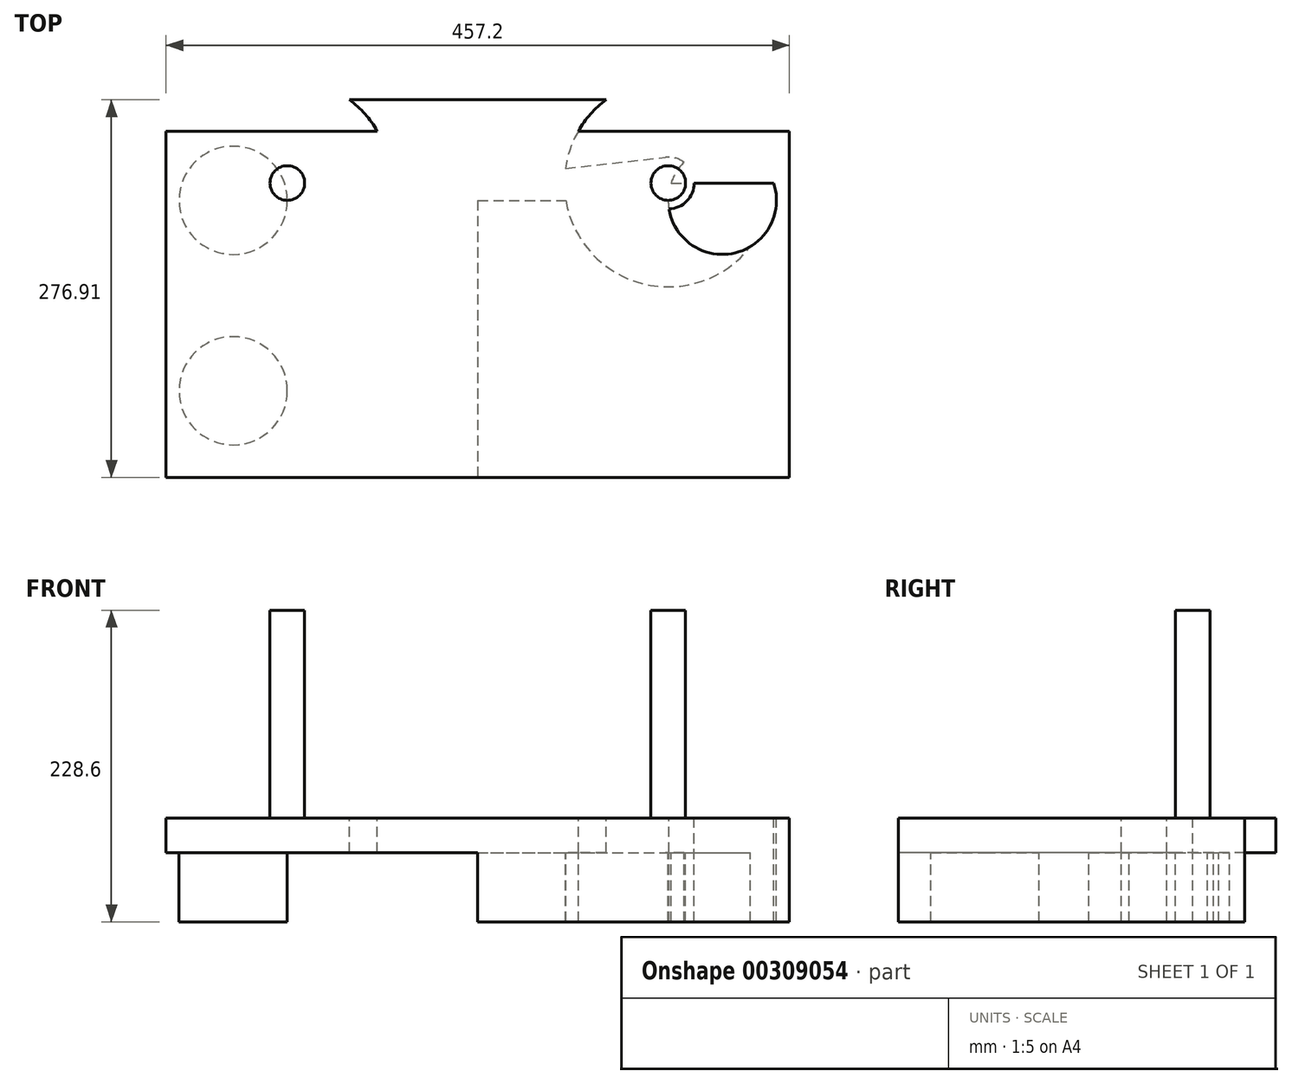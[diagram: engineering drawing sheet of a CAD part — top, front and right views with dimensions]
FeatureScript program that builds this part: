
annotation { "Feature Type Name" : "Feature", "Feature Type Description" : "" }
export const myFeature = defineFeature(function(context is Context, id is Id, definition is map)
    precondition{}
    {
        {
            var Q0;
            Q0=qCreatedBy(makeId("Top.planeOp"),FACE);
            var sketch = newSketch(context, id + "F0", { "sketchPlane" : qUnion([Q0])});
            skLineSegment(sketch, "E0", {"start": v(-140.58, 0) * mm, "end": v(0, 0) * mm});
            skLineSegment(sketch, "E1", {"start": v(0, 0) * mm, "end": v(140.58, 0) * mm});
            skLineSegment(sketch, "E2", {"start": v(0, 0) * mm, "end": v(139.7, 15.67) * mm});
            skLineSegment(sketch, "E3", {"start": v(0, 0) * mm, "end": v(-139.7, 15.67) * mm});
            skLineSegment(sketch, "E4.0", {"start": v(0, -57.5) * mm, "end": v(146.07, -41.12) * mm});
            skLineSegment(sketch, "E4.1", {"start": v(0, -57.5) * mm, "end": v(-146.07, -41.12) * mm});
            skLineSegment(sketch, "E5.0", {"start": v(0, 57.5) * mm, "end": v(-133.33, 72.46) * mm});
            skLineSegment(sketch, "E5.1", {"start": v(0, 57.5) * mm, "end": v(133.33, 72.46) * mm});
            skArc(sketch, "E6", {"start": v(-69.27, 108.43) * mm, "mid": v(0, 0.48) * mm, "end": v(69.27, 108.43) * mm});
            skCircle(sketch, "E7", {"center": v(0, 76.68) * mm, "radius": 19.05 * mm});
            skCircle(sketch, "E8", {"center": v(139.7, -61) * mm, "radius": 76.2 * mm});
            skCircle(sketch, "E9", {"center": v(-139.7, -61) * mm, "radius": 76.2 * mm});
            skCircle(sketch, "E10", {"center": v(139.7, -61) * mm, "radius": 19.05 * mm});
            skCircle(sketch, "E11", {"center": v(-139.7, -61) * mm, "radius": 19.05 * mm});
            skLineSegment(sketch, "E12", {"start": v(-139.7, 15.67) * mm, "end": v(139.7, 15.67) * mm});
            skCircle(sketch, "E13", {"center": v(0, 76.68) * mm, "radius": 12.7 * mm});
            skCircle(sketch, "E14", {"center": v(-139.7, -61) * mm, "radius": 12.7 * mm});
            skCircle(sketch, "E15", {"center": v(139.7, -61) * mm, "radius": 12.7 * mm});
            skLineSegment(sketch, "E16.bottom", {"start": v(-228.6, -22.9) * mm, "end": v(228.6, -22.9) * mm});
            skLineSegment(sketch, "E16.top", {"start": v(-228.6, -276.9) * mm, "end": v(228.6, -276.9) * mm});
            skLineSegment(sketch, "E16.left", {"start": v(-228.6, -22.9) * mm, "end": v(-228.6, -276.9) * mm});
            skLineSegment(sketch, "E16.right", {"start": v(228.6, -22.9) * mm, "end": v(228.6, -276.9) * mm});
            skLineSegment(sketch, "E17", {"start": v(-228.6, -61) * mm, "end": v(-139.7, -61) * mm});
            skLineSegment(sketch, "E18", {"start": v(139.7, -61) * mm, "end": v(228.6, -61) * mm});
            skLineSegment(sketch, "E19", {"start": v(0, -22.9) * mm, "end": v(0, -276.9) * mm});
            skLineSegment(sketch, "E20", {"start": v(-179.39, -73.7) * mm, "end": v(179.39, -73.7) * mm});
            skPoint(sketch, "E21", {"position": v(0, -73.7) * mm});
            skCircle(sketch, "E22", {"center": v(-179.39, -73.7) * mm, "radius": 39.69 * mm});
            skCircle(sketch, "E23", {"center": v(179.39, -73.7) * mm, "radius": 39.69 * mm});
            skLineSegment(sketch, "E24", {"start": v(-179.39, -213.4) * mm, "end": v(0, -213.4) * mm});
            skLineSegment(sketch, "E25", {"start": v(0, -213.4) * mm, "end": v(179.39, -213.4) * mm});
            skCircle(sketch, "E26", {"center": v(-179.39, -213.4) * mm, "radius": 39.69 * mm});
            skCircle(sketch, "E27", {"center": v(179.39, -213.4) * mm, "radius": 39.69 * mm});
            skLineSegment(sketch, "E28", {"start": v(294.3, 2.5) * mm, "end": v(418.12, 2.5) * mm});
            skLineSegment(sketch, "E29", {"start": v(-69.27, 108.43) * mm, "end": v(-30.16, 108.43) * mm});
            skLineSegment(sketch, "E30", {"start": v(-30.16, 108.43) * mm, "end": v(-30.16, 127.48) * mm});
            skLineSegment(sketch, "E31", {"start": v(-30.16, 127.48) * mm, "end": v(30.16, 127.48) * mm});
            skLineSegment(sketch, "E32", {"start": v(30.16, 127.48) * mm, "end": v(30.16, 108.43) * mm});
            skLineSegment(sketch, "E33", {"start": v(0, 108.43) * mm, "end": v(0, 127.48) * mm, "construction": true});
            skLineSegment(sketch, "E34.trimOffspring", {"start": v(30.16, 108.43) * mm, "end": v(69.27, 108.43) * mm});
            skSolve(sketch);
        }
        {
            var Q0;
            {var subQ0=sQuery(id+"F0.wireOp",EDGE,"E16.bottom");var subQ1=sQuery(id+"F0.wireOp",EDGE,"E8");var subQ2=makeQuery(id+"F0.imprint","INTERSECT",VERTEX,{"disambiguationData":[OD(0.0)],"derivedFrom":[subQ1,subQ0]});Q0=makeQuery(id+"F0.imprint","IMPRINT",FACE,{"disambiguationData":[TD([[makeQuery(id+"F0.imprint","IMPRINT",EDGE,{"disambiguationData":[TD([[subQ2,1.0]])],"derivedFrom":subQ1}),-1.0]])]});}
            var Q1;
            Q1=makeQuery(id+"F0.imprint","IMPRINT",FACE,{"disambiguationData":[TD([[makeQuery(id+"F0.imprint","IMPRINT",EDGE,{"derivedFrom":sQuery(id+"F0.wireOp",EDGE,"E27")}),-1.0]])]});
            var Q2;
            Q2=makeQuery(id+"F0.imprint","IMPRINT",FACE,{"disambiguationData":[TD([[makeQuery(id+"F0.imprint","IMPRINT",EDGE,{"derivedFrom":sQuery(id+"F0.wireOp",EDGE,"E26")}),-1.0]])]});
            var Q3;
            {var subQ0=sQuery(id+"F0.wireOp",EDGE,"E20");var subQ1=sQuery(id+"F0.wireOp",EDGE,"E8");var subQ2=makeQuery(id+"F0.imprint","INTERSECT",VERTEX,{"derivedFrom":[subQ1,subQ0]});Q3=makeQuery(id+"F0.imprint","IMPRINT",FACE,{"disambiguationData":[TD([[makeQuery(id+"F0.imprint","IMPRINT",EDGE,{"disambiguationData":[TD([[subQ2,-1.0]])],"derivedFrom":subQ1}),1.0]])]});}
            var Q4;
            {var subQ0=sQuery(id+"F0.wireOp",EDGE,"E23");var subQ1=sQuery(id+"F0.wireOp",EDGE,"E8");var subQ2=makeQuery(id+"F0.imprint","INTERSECT",VERTEX,{"disambiguationData":[OD(0.0)],"derivedFrom":[subQ1,subQ0]});Q4=makeQuery(id+"F0.imprint","IMPRINT",FACE,{"disambiguationData":[TD([[makeQuery(id+"F0.imprint","IMPRINT",EDGE,{"disambiguationData":[TD([[subQ2,-1.0]])],"derivedFrom":subQ1}),1.0]])]});}
            var Q5;
            Q5=makeQuery(id+"F0.imprint","IMPRINT",FACE,{"disambiguationData":[TD([[makeQuery(id+"F0.imprint","IMPRINT",EDGE,{"derivedFrom":sQuery(id+"F0.wireOp",EDGE,"E27")}),1.0]])]});
            var Q6;
            Q6=makeQuery(id+"F0.imprint","IMPRINT",FACE,{"disambiguationData":[TD([[makeQuery(id+"F0.imprint","IMPRINT",EDGE,{"derivedFrom":sQuery(id+"F0.wireOp",EDGE,"E26")}),1.0]])]});
            var Q7;
            {var subQ0=sQuery(id+"F0.wireOp",EDGE,"E23");var subQ1=sQuery(id+"F0.wireOp",EDGE,"E8");var subQ2=makeQuery(id+"F0.imprint","INTERSECT",VERTEX,{"disambiguationData":[OD(0.0)],"derivedFrom":[subQ1,subQ0]});Q7=makeQuery(id+"F0.imprint","IMPRINT",FACE,{"disambiguationData":[TD([[makeQuery(id+"F0.imprint","IMPRINT",EDGE,{"disambiguationData":[TD([[subQ2,-1.0]])],"derivedFrom":subQ1}),-1.0]])]});}
            var Q8;
            {var subQ0=sQuery(id+"F0.wireOp",EDGE,"E22");var subQ1=sQuery(id+"F0.wireOp",EDGE,"E9");var subQ2=makeQuery(id+"F0.imprint","INTERSECT",VERTEX,{"disambiguationData":[OD(0.0)],"derivedFrom":[subQ1,subQ0]});Q8=makeQuery(id+"F0.imprint","IMPRINT",FACE,{"disambiguationData":[TD([[makeQuery(id+"F0.imprint","IMPRINT",EDGE,{"disambiguationData":[TD([[subQ2,-1.0]])],"derivedFrom":subQ1}),-1.0]])]});}
            var Q9;
            {var subQ0=sQuery(id+"F0.wireOp",EDGE,"E16.bottom");var subQ1=sQuery(id+"F0.wireOp",EDGE,"E9");var subQ2=makeQuery(id+"F0.imprint","INTERSECT",VERTEX,{"disambiguationData":[OD(0.0)],"derivedFrom":[subQ1,subQ0]});Q9=makeQuery(id+"F0.imprint","IMPRINT",FACE,{"disambiguationData":[TD([[makeQuery(id+"F0.imprint","IMPRINT",EDGE,{"disambiguationData":[TD([[subQ2,-1.0]])],"derivedFrom":subQ1}),-1.0]])]});}
            var Q10;
            {var subQ1=sQuery(id+"F0.wireOp",EDGE,"E4.1");var subQ3=sQuery(id+"F0.wireOp",EDGE,"E9");var subQ4=makeQuery(id+"F0.imprint","INTERSECT",VERTEX,{"derivedFrom":[subQ1,subQ3]});Q10=makeQuery(id+"F0.imprint","IMPRINT",FACE,{"disambiguationData":[TD([[makeQuery(id+"F0.imprint","IMPRINT",EDGE,{"disambiguationData":[TD([[subQ4,1.0]])],"derivedFrom":subQ3}),-1.0]])]});}
            var Q11;
            {var subQ1=sQuery(id+"F0.wireOp",EDGE,"E4.0");var subQ3=sQuery(id+"F0.wireOp",EDGE,"E8");var subQ4=makeQuery(id+"F0.imprint","INTERSECT",VERTEX,{"derivedFrom":[subQ1,subQ3]});Q11=makeQuery(id+"F0.imprint","IMPRINT",FACE,{"disambiguationData":[TD([[makeQuery(id+"F0.imprint","IMPRINT",EDGE,{"disambiguationData":[TD([[subQ4,-1.0]])],"derivedFrom":subQ3}),-1.0]])]});}
            var Q12;
            {var subQ5=sQuery(id+"F0.wireOp",EDGE,"E10");var subQ6=sQuery(id+"F0.wireOp",EDGE,"E4.0");var subQ7=makeQuery(id+"F0.imprint","INTERSECT",VERTEX,{"derivedFrom":[subQ6,subQ5]});Q12=makeQuery(id+"F0.imprint","IMPRINT",FACE,{"disambiguationData":[TD([[makeQuery(id+"F0.imprint","IMPRINT",EDGE,{"disambiguationData":[TD([[subQ7,1.0]])],"derivedFrom":subQ6}),-1.0]])]});}
            var Q13;
            {var subQ0=sQuery(id+"F0.wireOp",EDGE,"E10");var subQ1=sQuery(id+"F0.wireOp",EDGE,"E4.0");var subQ2=makeQuery(id+"F0.imprint","INTERSECT",VERTEX,{"derivedFrom":[subQ1,subQ0]});Q13=makeQuery(id+"F0.imprint","IMPRINT",FACE,{"disambiguationData":[TD([[makeQuery(id+"F0.imprint","IMPRINT",EDGE,{"disambiguationData":[TD([[subQ2,1.0]])],"derivedFrom":subQ1}),1.0]])]});}
            var Q14;
            {var subQ1=sQuery(id+"F0.wireOp",EDGE,"E4.0");var subQ3=sQuery(id+"F0.wireOp",EDGE,"E8");var subQ4=makeQuery(id+"F0.imprint","INTERSECT",VERTEX,{"derivedFrom":[subQ1,subQ3]});Q14=makeQuery(id+"F0.imprint","IMPRINT",FACE,{"disambiguationData":[TD([[makeQuery(id+"F0.imprint","IMPRINT",EDGE,{"disambiguationData":[TD([[subQ4,1.0]])],"derivedFrom":subQ3}),-1.0]])]});}
            var Q15;
            {var subQ1=sQuery(id+"F0.wireOp",EDGE,"E4.1");var subQ3=sQuery(id+"F0.wireOp",EDGE,"E9");var subQ4=makeQuery(id+"F0.imprint","INTERSECT",VERTEX,{"derivedFrom":[subQ1,subQ3]});Q15=makeQuery(id+"F0.imprint","IMPRINT",FACE,{"disambiguationData":[TD([[makeQuery(id+"F0.imprint","IMPRINT",EDGE,{"disambiguationData":[TD([[subQ4,-1.0]])],"derivedFrom":subQ3}),-1.0]])]});}
            var Q16;
            {var subQ0=sQuery(id+"F0.wireOp",EDGE,"E11");var subQ1=sQuery(id+"F0.wireOp",EDGE,"E4.1");var subQ2=makeQuery(id+"F0.imprint","INTERSECT",VERTEX,{"derivedFrom":[subQ1,subQ0]});Q16=makeQuery(id+"F0.imprint","IMPRINT",FACE,{"disambiguationData":[TD([[makeQuery(id+"F0.imprint","IMPRINT",EDGE,{"disambiguationData":[TD([[subQ2,1.0]])],"derivedFrom":subQ1}),-1.0]])]});}
            var Q17;
            {var subQ0=sQuery(id+"F0.wireOp",EDGE,"E11");var subQ1=sQuery(id+"F0.wireOp",EDGE,"E4.1");var subQ2=makeQuery(id+"F0.imprint","INTERSECT",VERTEX,{"derivedFrom":[subQ1,subQ0]});Q17=makeQuery(id+"F0.imprint","IMPRINT",FACE,{"disambiguationData":[TD([[makeQuery(id+"F0.imprint","IMPRINT",EDGE,{"disambiguationData":[TD([[subQ2,1.0]])],"derivedFrom":subQ1}),1.0]])]});}
            var Q18;
            {var subQ0=sQuery(id+"F0.wireOp",EDGE,"E22");var subQ1=sQuery(id+"F0.wireOp",EDGE,"E9");var subQ2=makeQuery(id+"F0.imprint","INTERSECT",VERTEX,{"disambiguationData":[OD(1.0)],"derivedFrom":[subQ1,subQ0]});Q18=makeQuery(id+"F0.imprint","IMPRINT",FACE,{"disambiguationData":[TD([[makeQuery(id+"F0.imprint","IMPRINT",EDGE,{"disambiguationData":[TD([[subQ2,-1.0]])],"derivedFrom":subQ1}),1.0]])]});}
            var Q19;
            {var subQ0=sQuery(id+"F0.wireOp",EDGE,"E22");var subQ1=sQuery(id+"F0.wireOp",EDGE,"E9");var subQ2=makeQuery(id+"F0.imprint","INTERSECT",VERTEX,{"disambiguationData":[OD(0.0)],"derivedFrom":[subQ1,subQ0]});Q19=makeQuery(id+"F0.imprint","IMPRINT",FACE,{"disambiguationData":[TD([[makeQuery(id+"F0.imprint","IMPRINT",EDGE,{"disambiguationData":[TD([[subQ2,-1.0]])],"derivedFrom":subQ1}),1.0]])]});}
            var Q20;
            Q20=makeQuery(id+"F0.imprint","IMPRINT",FACE,{"disambiguationData":[TD([[makeQuery(id+"F0.imprint","IMPRINT",EDGE,{"derivedFrom":sQuery(id+"F0.wireOp",EDGE,"E14")}),-1.0]])]});
            var Q21;
            Q21=makeQuery(id+"F0.imprint","IMPRINT",FACE,{"disambiguationData":[TD([[makeQuery(id+"F0.imprint","IMPRINT",EDGE,{"derivedFrom":sQuery(id+"F0.wireOp",EDGE,"E14")}),1.0]])]});
            var Q22;
            Q22=makeQuery(id+"F0.imprint","IMPRINT",FACE,{"disambiguationData":[TD([[makeQuery(id+"F0.imprint","IMPRINT",EDGE,{"derivedFrom":sQuery(id+"F0.wireOp",EDGE,"E15")}),-1.0]])]});
            var Q23;
            Q23=makeQuery(id+"F0.imprint","IMPRINT",FACE,{"disambiguationData":[TD([[makeQuery(id+"F0.imprint","IMPRINT",EDGE,{"derivedFrom":sQuery(id+"F0.wireOp",EDGE,"E15")}),1.0]])]});
            var Q24;
            {var subQ0=sQuery(id+"F0.wireOp",EDGE,"E17");var subQ1=sQuery(id+"F0.wireOp",EDGE,"E9");var subQ2=makeQuery(id+"F0.imprint","INTERSECT",VERTEX,{"derivedFrom":[subQ1,subQ0]});Q24=makeQuery(id+"F0.imprint","IMPRINT",FACE,{"disambiguationData":[TD([[makeQuery(id+"F0.imprint","IMPRINT",EDGE,{"disambiguationData":[TD([[subQ2,-1.0]])],"derivedFrom":subQ1}),1.0]])]});}
            var Q25;
            {var subQ0=sQuery(id+"F0.wireOp",EDGE,"E17");var subQ1=sQuery(id+"F0.wireOp",EDGE,"E9");var subQ2=makeQuery(id+"F0.imprint","INTERSECT",VERTEX,{"derivedFrom":[subQ1,subQ0]});Q25=makeQuery(id+"F0.imprint","IMPRINT",FACE,{"disambiguationData":[TD([[makeQuery(id+"F0.imprint","IMPRINT",EDGE,{"disambiguationData":[TD([[subQ2,-1.0]])],"derivedFrom":subQ1}),-1.0]])]});}
            var Q26;
            {var subQ1=sQuery(id+"F0.wireOp",EDGE,"E11");var subQ7=makeQuery(id+"F0.imprint","INTERSECT",VERTEX,{"derivedFrom":[sQuery(id+"F0.wireOp",EDGE,"E4.1"),subQ1]});Q26=makeQuery(id+"F0.imprint","IMPRINT",FACE,{"disambiguationData":[TD([[makeQuery(id+"F0.imprint","IMPRINT",EDGE,{"disambiguationData":[TD([[subQ7,-1.0]])],"derivedFrom":subQ1}),1.0]])]});}
            var Q27;
            {var subQ0=sQuery(id+"F0.wireOp",EDGE,"E22");var subQ1=sQuery(id+"F0.wireOp",EDGE,"E11");var subQ2=makeQuery(id+"F0.imprint","INTERSECT",VERTEX,{"disambiguationData":[OD(1.0)],"derivedFrom":[subQ1,subQ0]});Q27=makeQuery(id+"F0.imprint","IMPRINT",FACE,{"disambiguationData":[TD([[makeQuery(id+"F0.imprint","IMPRINT",EDGE,{"disambiguationData":[TD([[subQ2,-1.0]])],"derivedFrom":subQ1}),1.0]])]});}
            var Q28;
            {var subQ1=sQuery(id+"F0.wireOp",EDGE,"E10");var subQ7=makeQuery(id+"F0.imprint","INTERSECT",VERTEX,{"derivedFrom":[sQuery(id+"F0.wireOp",EDGE,"E4.0"),subQ1]});Q28=makeQuery(id+"F0.imprint","IMPRINT",FACE,{"disambiguationData":[TD([[makeQuery(id+"F0.imprint","IMPRINT",EDGE,{"disambiguationData":[TD([[subQ7,1.0]])],"derivedFrom":subQ1}),1.0]])]});}
            var Q29;
            {var subQ0=sQuery(id+"F0.wireOp",EDGE,"E20");var subQ1=sQuery(id+"F0.wireOp",EDGE,"E11");var subQ2=makeQuery(id+"F0.imprint","INTERSECT",VERTEX,{"disambiguationData":[OD(0.0)],"derivedFrom":[subQ1,subQ0]});Q29=makeQuery(id+"F0.imprint","IMPRINT",FACE,{"disambiguationData":[TD([[makeQuery(id+"F0.imprint","IMPRINT",EDGE,{"disambiguationData":[TD([[subQ2,-1.0]])],"derivedFrom":subQ1}),1.0]])]});}
            var Q30;
            {var subQ0=sQuery(id+"F0.wireOp",EDGE,"E20");var subQ1=sQuery(id+"F0.wireOp",EDGE,"E10");var subQ2=makeQuery(id+"F0.imprint","INTERSECT",VERTEX,{"disambiguationData":[OD(1.0)],"derivedFrom":[subQ1,subQ0]});Q30=makeQuery(id+"F0.imprint","IMPRINT",FACE,{"disambiguationData":[TD([[makeQuery(id+"F0.imprint","IMPRINT",EDGE,{"disambiguationData":[TD([[subQ2,-1.0]])],"derivedFrom":subQ1}),1.0]])]});}
            var Q31;
            {var subQ0=sQuery(id+"F0.wireOp",EDGE,"E20");var subQ1=sQuery(id+"F0.wireOp",EDGE,"E10");var subQ2=makeQuery(id+"F0.imprint","INTERSECT",VERTEX,{"disambiguationData":[OD(0.0)],"derivedFrom":[subQ1,subQ0]});Q31=makeQuery(id+"F0.imprint","IMPRINT",FACE,{"disambiguationData":[TD([[makeQuery(id+"F0.imprint","IMPRINT",EDGE,{"disambiguationData":[TD([[subQ2,1.0]])],"derivedFrom":subQ1}),1.0]])]});}
            var Q32;
            {var subQ0=sQuery(id+"F0.wireOp",EDGE,"E18");var subQ1=sQuery(id+"F0.wireOp",EDGE,"E8");var subQ2=makeQuery(id+"F0.imprint","INTERSECT",VERTEX,{"derivedFrom":[subQ1,subQ0]});Q32=makeQuery(id+"F0.imprint","IMPRINT",FACE,{"disambiguationData":[TD([[makeQuery(id+"F0.imprint","IMPRINT",EDGE,{"disambiguationData":[TD([[subQ2,-1.0]])],"derivedFrom":subQ1}),1.0]])]});}
            extrude(context, id + "F1", {"entities" : qUnion([Q0, Q1, Q2, Q3, Q4, Q5, Q6, Q7, Q8, Q9, Q10, Q11, Q12, Q13, Q14, Q15, Q16, Q17, Q18, Q19, Q20, Q21, Q22, Q23, Q24, Q25, Q26, Q27, Q28, Q29, Q30, Q31, Q32]), "oppositeDirection" : true, "depth" : 25.4 * mm});
        }
        {
            var Q0;
            {var subQ0=sQuery(id+"F0.wireOp",EDGE,"E18");var subQ1=sQuery(id+"F0.wireOp",EDGE,"E8");var subQ2=makeQuery(id+"F0.imprint","INTERSECT",VERTEX,{"derivedFrom":[subQ1,subQ0]});Q0=makeQuery(id+"F0.imprint","IMPRINT",FACE,{"disambiguationData":[TD([[makeQuery(id+"F0.imprint","IMPRINT",EDGE,{"disambiguationData":[TD([[subQ2,-1.0]])],"derivedFrom":subQ1}),1.0]])]});}
            var Q1;
            {var subQ0=sQuery(id+"F0.wireOp",EDGE,"E18");var subQ1=sQuery(id+"F0.wireOp",EDGE,"E8");var subQ2=makeQuery(id+"F0.imprint","INTERSECT",VERTEX,{"derivedFrom":[subQ1,subQ0]});Q1=makeQuery(id+"F0.imprint","IMPRINT",FACE,{"disambiguationData":[TD([[makeQuery(id+"F0.imprint","IMPRINT",EDGE,{"disambiguationData":[TD([[subQ2,-1.0]])],"derivedFrom":subQ1}),-1.0]])]});}
            var Q2;
            {var subQ0=sQuery(id+"F0.wireOp",EDGE,"E23");var subQ1=sQuery(id+"F0.wireOp",EDGE,"E8");var subQ2=makeQuery(id+"F0.imprint","INTERSECT",VERTEX,{"disambiguationData":[OD(0.0)],"derivedFrom":[subQ1,subQ0]});Q2=makeQuery(id+"F0.imprint","IMPRINT",FACE,{"disambiguationData":[TD([[makeQuery(id+"F0.imprint","IMPRINT",EDGE,{"disambiguationData":[TD([[subQ2,-1.0]])],"derivedFrom":subQ1}),-1.0]])]});}
            var Q3;
            {var subQ1=sQuery(id+"F0.wireOp",EDGE,"E8");var subQ6=sQuery(id+"F0.wireOp",EDGE,"E23");var subQ8=makeQuery(id+"F0.imprint","INTERSECT",VERTEX,{"disambiguationData":[OD(0.0)],"derivedFrom":[subQ1,subQ6]});Q3=makeQuery(id+"F0.imprint","IMPRINT",FACE,{"disambiguationData":[TD([[makeQuery(id+"F0.imprint","IMPRINT",EDGE,{"disambiguationData":[TD([[subQ8,-1.0]])],"derivedFrom":subQ1}),1.0]])]});}
            var Q4;
            {var subQ0=sQuery(id+"F0.wireOp",EDGE,"E20");var subQ1=sQuery(id+"F0.wireOp",EDGE,"E10");var subQ2=makeQuery(id+"F0.imprint","INTERSECT",VERTEX,{"disambiguationData":[OD(0.0)],"derivedFrom":[subQ1,subQ0]});Q4=makeQuery(id+"F0.imprint","IMPRINT",FACE,{"disambiguationData":[TD([[makeQuery(id+"F0.imprint","IMPRINT",EDGE,{"disambiguationData":[TD([[subQ2,-1.0]])],"derivedFrom":subQ1}),1.0]])]});}
            var Q5;
            {var subQ0=sQuery(id+"F0.wireOp",EDGE,"E20");var subQ1=sQuery(id+"F0.wireOp",EDGE,"E10");var subQ2=makeQuery(id+"F0.imprint","INTERSECT",VERTEX,{"disambiguationData":[OD(0.0)],"derivedFrom":[subQ1,subQ0]});Q5=makeQuery(id+"F0.imprint","IMPRINT",FACE,{"disambiguationData":[TD([[makeQuery(id+"F0.imprint","IMPRINT",EDGE,{"disambiguationData":[TD([[subQ2,1.0]])],"derivedFrom":subQ1}),1.0]])]});}
            var Q6;
            {var subQ0=sQuery(id+"F0.wireOp",EDGE,"E18");var subQ3=sQuery(id+"F0.wireOp",EDGE,"E23");var subQ5=makeQuery(id+"F0.imprint","INTERSECT",VERTEX,{"disambiguationData":[OD(0.0)],"derivedFrom":[subQ0,subQ3]});Q6=makeQuery(id+"F0.imprint","IMPRINT",FACE,{"disambiguationData":[TD([[makeQuery(id+"F0.imprint","IMPRINT",EDGE,{"disambiguationData":[TD([[subQ5,-1.0]])],"derivedFrom":subQ0}),-1.0]])]});}
            var Q7;
            {var subQ0=sQuery(id+"F0.wireOp",EDGE,"E23");var subQ1=sQuery(id+"F0.wireOp",EDGE,"E15");var subQ2=makeQuery(id+"F0.imprint","INTERSECT",VERTEX,{"derivedFrom":[subQ1,subQ0]});Q7=makeQuery(id+"F0.imprint","IMPRINT",FACE,{"disambiguationData":[TD([[makeQuery(id+"F0.imprint","IMPRINT",EDGE,{"disambiguationData":[TD([[subQ2,1.0]])],"derivedFrom":subQ1}),1.0]])]});}
            var Q8;
            {var subQ0=sQuery(id+"F0.wireOp",EDGE,"E23");var subQ1=sQuery(id+"F0.wireOp",EDGE,"E10");var subQ2=makeQuery(id+"F0.imprint","INTERSECT",VERTEX,{"disambiguationData":[OD(0.0)],"derivedFrom":[subQ1,subQ0]});Q8=makeQuery(id+"F0.imprint","IMPRINT",FACE,{"disambiguationData":[TD([[makeQuery(id+"F0.imprint","IMPRINT",EDGE,{"disambiguationData":[TD([[subQ2,1.0]])],"derivedFrom":subQ1}),1.0]])]});}
            var Q9;
            Q9=makeQuery(id+"F0.imprint","IMPRINT",FACE,{"disambiguationData":[TD([[makeQuery(id+"F0.imprint","IMPRINT",EDGE,{"derivedFrom":sQuery(id+"F0.wireOp",EDGE,"E27")}),1.0]])]});
            var Q10;
            Q10=makeQuery(id+"F0.imprint","IMPRINT",FACE,{"disambiguationData":[TD([[makeQuery(id+"F0.imprint","IMPRINT",EDGE,{"derivedFrom":sQuery(id+"F0.wireOp",EDGE,"E26")}),1.0]])]});
            var Q11;
            {var subQ0=sQuery(id+"F0.wireOp",EDGE,"E17");var subQ1=sQuery(id+"F0.wireOp",EDGE,"E9");var subQ2=makeQuery(id+"F0.imprint","INTERSECT",VERTEX,{"derivedFrom":[subQ1,subQ0]});Q11=makeQuery(id+"F0.imprint","IMPRINT",FACE,{"disambiguationData":[TD([[makeQuery(id+"F0.imprint","IMPRINT",EDGE,{"disambiguationData":[TD([[subQ2,-1.0]])],"derivedFrom":subQ1}),-1.0]])]});}
            var Q12;
            {var subQ0=sQuery(id+"F0.wireOp",EDGE,"E22");var subQ1=sQuery(id+"F0.wireOp",EDGE,"E9");var subQ2=makeQuery(id+"F0.imprint","INTERSECT",VERTEX,{"disambiguationData":[OD(0.0)],"derivedFrom":[subQ1,subQ0]});Q12=makeQuery(id+"F0.imprint","IMPRINT",FACE,{"disambiguationData":[TD([[makeQuery(id+"F0.imprint","IMPRINT",EDGE,{"disambiguationData":[TD([[subQ2,-1.0]])],"derivedFrom":subQ1}),-1.0]])]});}
            var Q13;
            {var subQ0=sQuery(id+"F0.wireOp",EDGE,"E22");var subQ1=sQuery(id+"F0.wireOp",EDGE,"E9");var subQ2=makeQuery(id+"F0.imprint","INTERSECT",VERTEX,{"disambiguationData":[OD(0.0)],"derivedFrom":[subQ1,subQ0]});Q13=makeQuery(id+"F0.imprint","IMPRINT",FACE,{"disambiguationData":[TD([[makeQuery(id+"F0.imprint","IMPRINT",EDGE,{"disambiguationData":[TD([[subQ2,-1.0]])],"derivedFrom":subQ1}),1.0]])]});}
            var Q14;
            {var subQ0=sQuery(id+"F0.wireOp",EDGE,"E17");var subQ1=sQuery(id+"F0.wireOp",EDGE,"E9");var subQ2=makeQuery(id+"F0.imprint","INTERSECT",VERTEX,{"derivedFrom":[subQ1,subQ0]});Q14=makeQuery(id+"F0.imprint","IMPRINT",FACE,{"disambiguationData":[TD([[makeQuery(id+"F0.imprint","IMPRINT",EDGE,{"disambiguationData":[TD([[subQ2,-1.0]])],"derivedFrom":subQ1}),1.0]])]});}
            var Q15;
            {var subQ0=sQuery(id+"F0.wireOp",EDGE,"E22");var subQ1=sQuery(id+"F0.wireOp",EDGE,"E11");var subQ2=makeQuery(id+"F0.imprint","INTERSECT",VERTEX,{"disambiguationData":[OD(0.0)],"derivedFrom":[subQ1,subQ0]});Q15=makeQuery(id+"F0.imprint","IMPRINT",FACE,{"disambiguationData":[TD([[makeQuery(id+"F0.imprint","IMPRINT",EDGE,{"disambiguationData":[TD([[subQ2,-1.0]])],"derivedFrom":subQ1}),1.0]])]});}
            var Q16;
            {var subQ0=sQuery(id+"F0.wireOp",EDGE,"E17");var subQ1=sQuery(id+"F0.wireOp",EDGE,"E14");var subQ2=makeQuery(id+"F0.imprint","INTERSECT",VERTEX,{"derivedFrom":[subQ1,subQ0]});Q16=makeQuery(id+"F0.imprint","IMPRINT",FACE,{"disambiguationData":[TD([[makeQuery(id+"F0.imprint","IMPRINT",EDGE,{"disambiguationData":[TD([[subQ2,1.0]])],"derivedFrom":subQ1}),1.0]])]});}
            var Q17;
            {var subQ0=sQuery(id+"F0.wireOp",EDGE,"E20");var subQ1=sQuery(id+"F0.wireOp",EDGE,"E11");var subQ2=makeQuery(id+"F0.imprint","INTERSECT",VERTEX,{"disambiguationData":[OD(0.0)],"derivedFrom":[subQ1,subQ0]});Q17=makeQuery(id+"F0.imprint","IMPRINT",FACE,{"disambiguationData":[TD([[makeQuery(id+"F0.imprint","IMPRINT",EDGE,{"disambiguationData":[TD([[subQ2,1.0]])],"derivedFrom":subQ1}),1.0]])]});}
            var Q18;
            {var subQ0=sQuery(id+"F0.wireOp",EDGE,"E17");var subQ3=sQuery(id+"F0.wireOp",EDGE,"E22");var subQ5=makeQuery(id+"F0.imprint","INTERSECT",VERTEX,{"disambiguationData":[OD(0.0)],"derivedFrom":[subQ0,subQ3]});Q18=makeQuery(id+"F0.imprint","IMPRINT",FACE,{"disambiguationData":[TD([[makeQuery(id+"F0.imprint","IMPRINT",EDGE,{"disambiguationData":[TD([[subQ5,1.0]])],"derivedFrom":subQ0}),-1.0]])]});}
            var Q19;
            {var subQ0=sQuery(id+"F0.wireOp",EDGE,"E20");var subQ1=sQuery(id+"F0.wireOp",EDGE,"E11");var subQ2=makeQuery(id+"F0.imprint","INTERSECT",VERTEX,{"disambiguationData":[OD(0.0)],"derivedFrom":[subQ1,subQ0]});Q19=makeQuery(id+"F0.imprint","IMPRINT",FACE,{"disambiguationData":[TD([[makeQuery(id+"F0.imprint","IMPRINT",EDGE,{"disambiguationData":[TD([[subQ2,-1.0]])],"derivedFrom":subQ1}),1.0]])]});}
            extrude(context, id + "F2", {"entities" : qUnion([Q0, Q1, Q2, Q3, Q4, Q5, Q6, Q7, Q8, Q9, Q10, Q11, Q12, Q13, Q14, Q15, Q16, Q17, Q18, Q19]), "operationType" : NewBodyOperationType.ADD, "oppositeDirection" : true, "depth" : 76.2 * mm});
        }
        {
            var Q0;
            Q0=makeQuery(id+"F0.imprint","IMPRINT",FACE,{"disambiguationData":[TD([[makeQuery(id+"F0.imprint","IMPRINT",EDGE,{"derivedFrom":sQuery(id+"F0.wireOp",EDGE,"E14")}),1.0]])]});
            var Q1;
            Q1=makeQuery(id+"F0.imprint","IMPRINT",FACE,{"disambiguationData":[TD([[makeQuery(id+"F0.imprint","IMPRINT",EDGE,{"derivedFrom":sQuery(id+"F0.wireOp",EDGE,"E15")}),1.0]])]});
            extrude(context, id + "F3", {"entities" : qUnion([Q0, Q1]), "operationType" : NewBodyOperationType.ADD, "depth" : 152.4 * mm});
        }
    });
